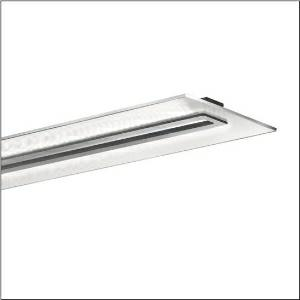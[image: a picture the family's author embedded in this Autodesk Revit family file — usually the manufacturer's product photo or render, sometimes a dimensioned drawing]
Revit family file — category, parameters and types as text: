
# Revit family: vega_r__11_5mn238dle003_bbe2
name_source: partatom
category: Lighting Fixtures
units: mm (PartAtom-declared; Revit-internal decimal feet)

## family parameters
Cut with Voids When Loaded = No
Host = Face
Light Source = No
Part Type = Normal
Room Calculation Point = No
Round Connector Dimension = Use Diameter
Shared = No

## types (1)
- --- (1 x LED 3000K / CRI = 80 (unbekannt), 7300 lm, 3000K)
    Apparent Load = 62 VA
    CIE Flux Codes = 61 86 97 62 100
    Color Rendering = 80
    Color Temperature = 3000K
    Default Elevation = 1800 mm
    Description = Vega® 11, office luminaire, primary light control with prismatic reflector, of PMMA, transparent prismatic structure, CAT 2 (L<= 1500cd/m²), light emission: direct/indirect distribution, primary light characteristic: symmetric, installation type: suspended mounting, surface-mounted, LED rated luminous flux: 7.300 lm, light colour: 830, colour temperature: 3000K, control gear: ECG, with terminal, 3+2-pole, max. 2.5mm², mains connection: 230V, AC, 50Hz, connection cable inclusive, cable length: 1,5 m, rated input power: 62W, luminaire housing, rectangular, rounded, of aluminium section, anodised, metallic grey (RAL 9006), length: 1.250 mm, width: 350 mm, height: 43mm, luminaire housing, lower part, of aluminium section, anodised, metallic grey (RAL 9006), of PC, grey, protection rating (complete): IP20, insulation class (complete): insulation class I (protective earthing), certification: CE, standard: EN 50419, packaging unit: 1 piece
    Height = 40 mm  [stored 0.131234 ft]
    Lamp = 1 x LED 3000K / CRI >= 80 (unbekannt)
    Lamp Light Flux = 7300 lm
    Lamp count = 1
    Length = 1250 mm
    Luminous efficacy = 118 lm/W
    Manufacturer = Siteco
    ModVariant = No
    Model = 5MN238DLE003
    Mounting Place = Ceiling
    Mounting Type = Pendant
    Number of Poles = 1
    OnlyDefault = Yes
    Power Factor = 1
    Product Name = Vega® 11
    Product group = office luminaire | ceiling pendant
    ProductGroupID = 905
    Protection Class = Protection class I
    Protection Degree = IP 20
    RLX_Detail_Level = 1
    RlxData = <blob elided: 62657 chars, md5=ef8f6063>
    Socket = socket
    Standby Power = 0 W
    System Light Flux = 7300 lm
    System Power = 62 W
    Type Comments = factory setting: luminous flux: 100 % | dim-lin: 254 | 460 mA
    Type Image = l_1004807.jpg
    URL = http://relux.com
    VarID = @adj_147209
    Voltage = 0 V
    Weight = 0.00 kg
    Width = 350 mm

note: [stored X ft] marks values corroborated as IEEE doubles in the binary element streams (Revit-internal decimal feet)

## geometry (parser evidence)
native form markers: Blend x4, Sweep x12
no freeform markers — native parametric forms only
